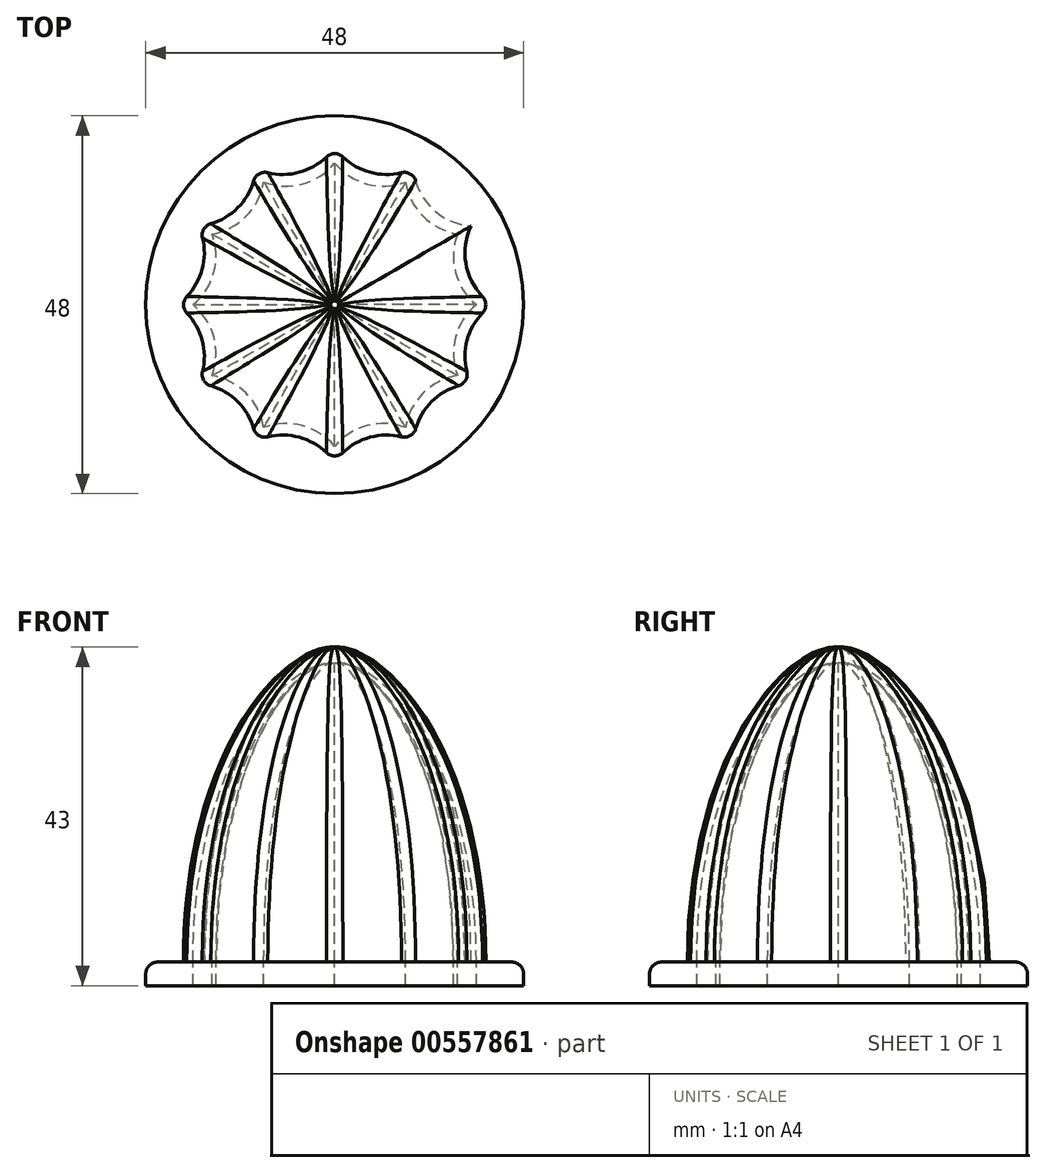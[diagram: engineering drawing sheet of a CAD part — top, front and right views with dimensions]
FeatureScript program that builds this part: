
annotation { "Feature Type Name" : "Feature", "Feature Type Description" : "" }
export const myFeature = defineFeature(function(context is Context, id is Id, definition is map)
    precondition{}
    {
        {
            var Q0;
            Q0=qCreatedBy(makeId("Top.planeOp"),FACE);
            var sketch = newSketch(context, id + "F0", { "sketchPlane" : qUnion([Q0])});
            skLineSegment(sketch, "E0", {"start": v(0, 0) * mm, "end": v(20, 0) * mm});
            skCircle(sketch, "E1.cCircle", {"center": v(0, 0) * mm, "radius": 20 * mm, "construction": true});
            skArc(sketch, "E2", {"start": v(-17.32, -10) * mm, "mid": v(-16.82, -4.5) * mm, "end": v(-20, 0) * mm});
            skArc(sketch, "E3.1.0", {"start": v(-10, -17.32) * mm, "mid": v(-12.32, -12.32) * mm, "end": v(-17.32, -10) * mm});
            skArc(sketch, "E3.2.0", {"start": v(0, -20) * mm, "mid": v(-4.5, -16.82) * mm, "end": v(-10, -17.32) * mm});
            skArc(sketch, "E3.3.0", {"start": v(10, -17.32) * mm, "mid": v(4.5, -16.82) * mm, "end": v(0, -20) * mm});
            skArc(sketch, "E3.4.0", {"start": v(17.32, -10) * mm, "mid": v(12.32, -12.32) * mm, "end": v(10, -17.32) * mm});
            skArc(sketch, "E3.5.0", {"start": v(20, 0) * mm, "mid": v(16.82, -4.5) * mm, "end": v(17.32, -10) * mm});
            skArc(sketch, "E3.6.0", {"start": v(17.32, 10) * mm, "mid": v(16.82, 4.5) * mm, "end": v(20, 0) * mm});
            skArc(sketch, "E3.7.0", {"start": v(10, 17.32) * mm, "mid": v(12.32, 12.32) * mm, "end": v(17.32, 10) * mm});
            skArc(sketch, "E3.8.0", {"start": v(0, 20) * mm, "mid": v(4.5, 16.82) * mm, "end": v(10, 17.32) * mm});
            skArc(sketch, "E3.9.0", {"start": v(-10, 17.32) * mm, "mid": v(-4.5, 16.82) * mm, "end": v(0, 20) * mm});
            skArc(sketch, "E3.10.0", {"start": v(-17.32, 10) * mm, "mid": v(-12.32, 12.32) * mm, "end": v(-10, 17.32) * mm});
            skArc(sketch, "E3.11.0", {"start": v(-20, 0) * mm, "mid": v(-16.82, 4.5) * mm, "end": v(-17.32, 10) * mm});
            skSolve(sketch);
        }
        {
            var Q0;
            Q0=qCreatedBy(makeId("Top.planeOp"),FACE);
            cPlane(context, id + "F1", {"entities" : qUnion([Q0]), "cplaneType" : CPlaneType.OFFSET, "offset" : 40 * mm, "width" : 150 * mm, "height" : 150 * mm});
        }
        {
            var Q0;
            Q0=qCreatedBy(id+"F1.planeOp",FACE);
            var sketch = newSketch(context, id + "F2", { "sketchPlane" : qUnion([Q0])});
            skCircle(sketch, "E4", {"center": v(0, 0) * mm, "radius": 0.5 * mm});
            skSolve(sketch);
        }
        {
            var Q0;
            Q0=makeQuery(id+"F0.imprint","IMPRINT",FACE,{"disambiguationData":[TD([[makeQuery(id+"F0.imprint","IMPRINT",EDGE,{"derivedFrom":sQuery(id+"F0.wireOp",EDGE,"E2")}),-1.0]])]});
            var Q1;
            Q1=makeQuery(id+"F2.imprint","IMPRINT",FACE,{"disambiguationData":[TD([[makeQuery(id+"F2.imprint","IMPRINT",EDGE,{"derivedFrom":sQuery(id+"F2.wireOp",EDGE,"E4")}),1.0]])]});
            loft(context, id + "F3", {"startCondition" : LoftEndDerivativeType.NORMAL_TO_PROFILE, "startMagnitude" : 2, "endCondition" : LoftEndDerivativeType.TANGENT_TO_PROFILE, "endMagnitude" : 1, "sheetProfilesArray" : [{ "sheetProfileEntities" : qUnion([Q0]) }, { "sheetProfileEntities" : qUnion([Q1]) }]});
        }
        {
            var Q0;
            Q0=makeQuery(id+"F3.opLoft","SWEPT_EDGE",EDGE,{"disambiguationData":[OSD([sQuery(id+"F0.wireOp",EDGE,"E3.1.0"),sQuery(id+"F0.wireOp",EDGE,"E3.2.0"),sQuery(id+"F0.wireOp",EDGE,"E3.3.0"),sQuery(id+"F2.wireOp",EDGE,"E4")])]});
            var Q1;
            Q1=makeQuery(id+"F3.opLoft","SWEPT_EDGE",EDGE,{"disambiguationData":[OSD([sQuery(id+"F0.wireOp",EDGE,"E3.2.0"),sQuery(id+"F0.wireOp",EDGE,"E3.3.0"),sQuery(id+"F0.wireOp",EDGE,"E3.4.0"),sQuery(id+"F2.wireOp",EDGE,"E4")])]});
            var Q2;
            Q2=makeQuery(id+"F3.opLoft","SWEPT_EDGE",EDGE,{"disambiguationData":[OSD([sQuery(id+"F0.wireOp",EDGE,"E3.3.0"),sQuery(id+"F0.wireOp",EDGE,"E3.4.0"),sQuery(id+"F0.wireOp",EDGE,"E3.5.0"),sQuery(id+"F2.wireOp",EDGE,"E4")])]});
            var Q3;
            Q3=makeQuery(id+"F3.opLoft","SWEPT_EDGE",EDGE,{"disambiguationData":[OSD([sQuery(id+"F0.wireOp",EDGE,"E3.5.0"),sQuery(id+"F0.wireOp",EDGE,"E3.6.0")])]});
            var Q4;
            Q4=makeQuery(id+"F3.opLoft","SWEPT_EDGE",EDGE,{"disambiguationData":[OSD([sQuery(id+"F0.wireOp",EDGE,"E3.5.0"),sQuery(id+"F0.wireOp",EDGE,"E3.6.0"),sQuery(id+"F0.wireOp",EDGE,"E3.7.0"),sQuery(id+"F2.wireOp",EDGE,"E4")])]});
            var Q5;
            Q5=makeQuery(id+"F3.opLoft","SWEPT_EDGE",EDGE,{"disambiguationData":[OSD([sQuery(id+"F0.wireOp",EDGE,"E3.6.0"),sQuery(id+"F0.wireOp",EDGE,"E3.7.0"),sQuery(id+"F0.wireOp",EDGE,"E3.8.0"),sQuery(id+"F2.wireOp",EDGE,"E4")])]});
            var Q6;
            Q6=makeQuery(id+"F3.opLoft","SWEPT_EDGE",EDGE,{"disambiguationData":[OSD([sQuery(id+"F0.wireOp",EDGE,"E2"),sQuery(id+"F0.wireOp",EDGE,"E3.1.0"),sQuery(id+"F0.wireOp",EDGE,"E3.2.0"),sQuery(id+"F2.wireOp",EDGE,"E4")])]});
            var Q7;
            Q7=makeQuery(id+"F3.opLoft","SWEPT_EDGE",EDGE,{"disambiguationData":[OSD([sQuery(id+"F0.wireOp",EDGE,"E2"),sQuery(id+"F0.wireOp",EDGE,"E3.1.0"),sQuery(id+"F0.wireOp",EDGE,"E3.11.0"),sQuery(id+"F2.wireOp",EDGE,"E4")])]});
            var Q8;
            Q8=makeQuery(id+"F3.opLoft","SWEPT_EDGE",EDGE,{"disambiguationData":[OSD([sQuery(id+"F0.wireOp",EDGE,"E2"),sQuery(id+"F0.wireOp",EDGE,"E3.10.0"),sQuery(id+"F0.wireOp",EDGE,"E3.11.0"),sQuery(id+"F2.wireOp",EDGE,"E4")])]});
            var Q9;
            Q9=makeQuery(id+"F3.opLoft","SWEPT_EDGE",EDGE,{"disambiguationData":[OSD([sQuery(id+"F0.wireOp",EDGE,"E3.9.0"),sQuery(id+"F0.wireOp",EDGE,"E3.10.0"),sQuery(id+"F0.wireOp",EDGE,"E3.11.0"),sQuery(id+"F2.wireOp",EDGE,"E4")])]});
            var Q10;
            Q10=makeQuery(id+"F3.opLoft","SWEPT_EDGE",EDGE,{"disambiguationData":[OSD([sQuery(id+"F0.wireOp",EDGE,"E3.8.0"),sQuery(id+"F0.wireOp",EDGE,"E3.9.0"),sQuery(id+"F0.wireOp",EDGE,"E3.10.0"),sQuery(id+"F2.wireOp",EDGE,"E4")])]});
            var Q11;
            Q11=makeQuery(id+"F3.opLoft","SWEPT_EDGE",EDGE,{"disambiguationData":[OSD([sQuery(id+"F0.wireOp",EDGE,"E3.7.0"),sQuery(id+"F0.wireOp",EDGE,"E3.8.0"),sQuery(id+"F0.wireOp",EDGE,"E3.9.0"),sQuery(id+"F2.wireOp",EDGE,"E4")])]});
            fillet(context, id + "F4", {"entities" : qUnion([Q0, Q1, Q2, Q3, Q4, Q5, Q6, Q7, Q8, Q9, Q10, Q11]), "radius" : 1.5 * mm, "tangentPropagation" : true, "allowEdgeOverflow" : false});
        }
        {
            var Q0;
            Q0=qCreatedBy(makeId("Top.planeOp"),FACE);
            var sketch = newSketch(context, id + "F5", { "sketchPlane" : qUnion([Q0])});
            skLineSegment(sketch, "E5", {"start": v(0, 0) * mm, "end": v(18, 0) * mm});
            skCircle(sketch, "E6.cCircle", {"center": v(0, 0) * mm, "radius": 18 * mm, "construction": true});
            skArc(sketch, "E7", {"start": v(-15.59, -9) * mm, "mid": v(-15.35, -4.11) * mm, "end": v(-18, 0) * mm});
            skArc(sketch, "E8.1.0", {"start": v(-9, -15.59) * mm, "mid": v(-11.24, -11.24) * mm, "end": v(-15.59, -9) * mm});
            skArc(sketch, "E8.2.0", {"start": v(0, -18) * mm, "mid": v(-4.11, -15.35) * mm, "end": v(-9, -15.59) * mm});
            skArc(sketch, "E8.3.0", {"start": v(9, -15.59) * mm, "mid": v(4.11, -15.35) * mm, "end": v(0, -18) * mm});
            skArc(sketch, "E8.4.0", {"start": v(15.59, -9) * mm, "mid": v(11.24, -11.24) * mm, "end": v(9, -15.59) * mm});
            skArc(sketch, "E8.5.0", {"start": v(18, 0) * mm, "mid": v(15.35, -4.11) * mm, "end": v(15.59, -9) * mm});
            skArc(sketch, "E8.6.0", {"start": v(15.59, 9) * mm, "mid": v(15.35, 4.11) * mm, "end": v(18, 0) * mm});
            skArc(sketch, "E8.7.0", {"start": v(9, 15.59) * mm, "mid": v(11.24, 11.24) * mm, "end": v(15.59, 9) * mm});
            skArc(sketch, "E8.8.0", {"start": v(0, 18) * mm, "mid": v(4.11, 15.35) * mm, "end": v(9, 15.59) * mm});
            skArc(sketch, "E8.9.0", {"start": v(-9, 15.59) * mm, "mid": v(-4.11, 15.35) * mm, "end": v(0, 18) * mm});
            skArc(sketch, "E8.10.0", {"start": v(-15.59, 9) * mm, "mid": v(-11.24, 11.24) * mm, "end": v(-9, 15.59) * mm});
            skArc(sketch, "E8.11.0", {"start": v(-18, 0) * mm, "mid": v(-15.35, 4.11) * mm, "end": v(-15.59, 9) * mm});
            skSolve(sketch);
        }
        {
            var Q0;
            Q0=qCreatedBy(makeId("Top.planeOp"),FACE);
            cPlane(context, id + "F6", {"entities" : qUnion([Q0]), "cplaneType" : CPlaneType.OFFSET, "offset" : 38 * mm, "width" : 150 * mm, "height" : 150 * mm});
        }
        {
            var Q0;
            Q0=qCreatedBy(id+"F6.planeOp",FACE);
            var sketch = newSketch(context, id + "F7", { "sketchPlane" : qUnion([Q0])});
            skCircle(sketch, "E9", {"center": v(0, 0) * mm, "radius": 0.5 * mm});
            skSolve(sketch);
        }
        {
            var Q1;
            Q1=makeQuery(id+"F5.imprint","IMPRINT",FACE,{"disambiguationData":[TD([[makeQuery(id+"F5.imprint","IMPRINT",EDGE,{"derivedFrom":sQuery(id+"F5.wireOp",EDGE,"E7")}),-1.0]])]});
            var Q2;
            Q2 = qSketchRegion(id + "F7", true);
            loft(context, id + "F8", {"operationType" : NewBodyOperationType.REMOVE, "startCondition" : LoftEndDerivativeType.NORMAL_TO_PROFILE, "startMagnitude" : 2, "endCondition" : LoftEndDerivativeType.TANGENT_TO_PROFILE, "endMagnitude" : 1, "sheetProfilesArray" : [{ "sheetProfileEntities" : qUnion([Q1]) }, { "sheetProfileEntities" : qUnion([Q2]) }]});
        }
        {
            var Q0;
            Q0=qCreatedBy(makeId("Top.planeOp"),FACE);
            var sketch = newSketch(context, id + "F9", { "sketchPlane" : qUnion([Q0])});
            skLineSegment(sketch, "E10", {"start": v(0, 0) * mm, "end": v(18, 0) * mm});
            skCircle(sketch, "E11.cCircle", {"center": v(0, 0) * mm, "radius": 18 * mm, "construction": true});
            skArc(sketch, "E12", {"start": v(-15.59, -9) * mm, "mid": v(-15.35, -4.11) * mm, "end": v(-18, 0) * mm});
            skArc(sketch, "E13.1.0", {"start": v(-9, -15.59) * mm, "mid": v(-11.24, -11.24) * mm, "end": v(-15.59, -9) * mm});
            skArc(sketch, "E13.2.0", {"start": v(0, -18) * mm, "mid": v(-4.11, -15.35) * mm, "end": v(-9, -15.59) * mm});
            skArc(sketch, "E13.3.0", {"start": v(9, -15.59) * mm, "mid": v(4.11, -15.35) * mm, "end": v(0, -18) * mm});
            skArc(sketch, "E13.4.0", {"start": v(15.59, -9) * mm, "mid": v(11.24, -11.24) * mm, "end": v(9, -15.59) * mm});
            skArc(sketch, "E13.5.0", {"start": v(18, 0) * mm, "mid": v(15.35, -4.11) * mm, "end": v(15.59, -9) * mm});
            skArc(sketch, "E13.6.0", {"start": v(15.59, 9) * mm, "mid": v(15.35, 4.11) * mm, "end": v(18, 0) * mm});
            skArc(sketch, "E13.7.0", {"start": v(9, 15.59) * mm, "mid": v(11.24, 11.24) * mm, "end": v(15.59, 9) * mm});
            skArc(sketch, "E13.8.0", {"start": v(0, 18) * mm, "mid": v(4.11, 15.35) * mm, "end": v(9, 15.59) * mm});
            skArc(sketch, "E13.9.0", {"start": v(-9, 15.59) * mm, "mid": v(-4.11, 15.35) * mm, "end": v(0, 18) * mm});
            skArc(sketch, "E13.10.0", {"start": v(-15.59, 9) * mm, "mid": v(-11.24, 11.24) * mm, "end": v(-9, 15.59) * mm});
            skArc(sketch, "E13.11.0", {"start": v(-18, 0) * mm, "mid": v(-15.35, 4.11) * mm, "end": v(-15.59, 9) * mm});
            skCircle(sketch, "E14", {"center": v(0, 0) * mm, "radius": 24 * mm});
            skSolve(sketch);
        }
        {
            var Q0;
            Q0=makeQuery(id+"F9.imprint","IMPRINT",FACE,{"disambiguationData":[TD([[makeQuery(id+"F9.imprint","IMPRINT",EDGE,{"derivedFrom":sQuery(id+"F9.wireOp",EDGE,"E12")}),1.0]])]});
            extrude(context, id + "F10", {"entities" : qUnion([Q0]), "operationType" : NewBodyOperationType.ADD, "oppositeDirection" : true, "depth" : 3 * mm, "offsetDistance" : 25 * mm});
        }
        {
            var Q0;
            Q0=makeQuery(id+"F10.opExtrude","CAP_EDGE",EDGE,{"disambiguationData":[OSD([sQuery(id+"F9.wireOp",EDGE,"E14")])],"isStart":true});
            fillet(context, id + "F11", {"entities" : qUnion([Q0]), "radius" : 1.5 * mm, "tangentPropagation" : true, "allowEdgeOverflow" : false});
        }
    });
